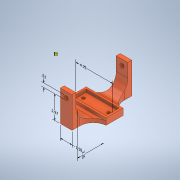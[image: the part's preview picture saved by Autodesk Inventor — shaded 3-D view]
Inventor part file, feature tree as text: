
AUTODESK INVENTOR PART (.ipt)
format: ipt  version: 2022.2 (Build 262287000, 287)  size: 1,950,720 bytes
history: native  units: in
note: dims shown in document units (in); Inventor stores cm internally (conversion verified against a paired STEP export)
features: other x6, sketch x6, extrude x6, fillet x2, hole x1, mirror x1
ambient origin geometry x8: Origin, YZ Plane, XZ Plane, XY Plane, X Axis, Y Axis, Z Axis, Center Point
bodies: Solid1 (feature_tree)
feature tree (22):
  other  "Annotations"
  sketch  "Sketch1"  dims[d0=1.7in d1=4.25in]
  extrude  "Extrusion1"  Depth=4.25in
  extrude  "Extrusion2"  Depth=0.25in
  hole  "Hole1"  [1 undecoded]
  extrude  "Extrusion10"  TaperAngle=0.0deg  [1 undecoded]
  extrude  "Extrusion11"  Depth=0.5in
  extrude  "Extrusion12"  Depth=0.05in
  mirror  "Mirror8"
  fillet  "Fillet1"  Radius=0.375in
  fillet  "Fillet2"  Radius=2.75in
  extrude  "Extrusion13"  Depth=0.05in
  sketch  "Sketch2"  dims[d2=0.25in d3=0.25in]
  sketch  "Sketch15"  dims[d4=0.475in d5=0.0in]
  sketch  "Sketch16"  dims[d6=0.35in d7=0.0in]
  sketch  "Sketch17"  dims[d8=0.5in d9=0.5in]
  sketch  "Sketch18"  dims[d10=0.201in d11=0.75in d12=0.4in d13=0.1in d14=0.5635in d15=1.0in d16=0.8108in d17=0.375in d24=0.375in d101=2.75in d102=0.0in d103=0.5in d104=3.5in d105=0.0in d109=1.5in d115=0.0in d116=0.0in d117=1.75in d118=1.75in d120=0.51in d140=0.05in d141=0.0in d142=3.225in d106=0.9428in d107=4.2237in d108=3.35in d110=0.3497in d111=0.335in d112=1.5in d125=0.0966in d126=0.3041in d127=2.97in d143=0.1201in d144=0.2095in d145=0.51in d92=0.237in d93=0.16in d94=4.75in d119=0.5in d121=0.5in d122=0.0344in]
  other  "Linear Dimension 1"
  other  "Linear Dimension 4"
  other  "Linear Dimension 5"
  other  "Linear Dimension 6"
  other  "Linear Dimension 7"
note: 2 required parameter values undecoded (feature->parameter linkage not recoverable at this tier; creation-order binding heuristic only, values carry confidence <= 0.55)
